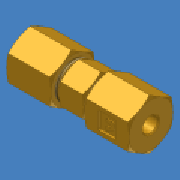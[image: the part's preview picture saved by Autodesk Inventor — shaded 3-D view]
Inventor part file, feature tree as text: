
AUTODESK INVENTOR PART (.ipt)
format: ipt  version: 2017 (Build 210142000, 142)  size: 289,792 bytes
history: native  units: in
note: dims shown in document units (in); Inventor stores cm internally (conversion verified against a paired STEP export)
features: other x2, sketch x1, imported_body x1
ambient origin geometry x8: Origin, YZ Plane, XZ Plane, XY Plane, X Axis, Y Axis, Z Axis, Center Point
bodies: Solid1 (feature_tree)
feature tree (4):
  other  "Table"
  other  "Union 62C.ipt"
  sketch  "Sketch1"
  imported_body  "DerivedBody::Union 62C.ipt"
